# Revit family: Equinox_168 Indirect + trim
name_source: partatom
category: Lighting Fixtures
revit_build: Autodesk Revit 2018 (Build: 20170223_1515(x64)
units: mm (PartAtom-declared; Revit-internal decimal feet)

## family parameters
Cut with Voids When Loaded = No
Host = Face
Light Source = Yes
OmniClass Number = 23.80.70.00
OmniClass Title = Lighting
Part Type = Normal
Room Calculation Point = No
Round Connector Dimension = Use Diameter
Shared = No

## types (1)
- 2059936 EQNX 165 2300 930 SSC
    Apparent Load = 20 VA
    Assembly Code = D5020200
    AssetType = Fixed
    ClassificationName = Uniclass2015
    ClassificationValue = EF_70_80
    Color Filter = 16777215
    Cost = 0 $
    Default Elevation = 1219 mm
    Description = Equinox is an elegant and innovative luminaire designed using the latest optical technology. It is a high quality and efficient lighting solution for office, hospitality, and retail environments. It creates inspirational halo effects regulated by a unique adjustable optic system. It is  Sylsmart dimmable downlight luminaire, Colour rendering index Ra >90, Colour temperature: 3000K Warm White, Class II, Cut out dimensions: 165mm. Low Glare UGR<19.
    Dimming Lamp Color Temperature Shift = <None>
    DocumentationLiterature = http://www.sylvania-lighting.com
    DurationUnit = hours
    ElectricShockClassification = 115
    Emit Shape Visible in Rendering = No
    Emit from Circle Diameter = 610 mm
    ExpectedLife = 50000
    Height (Max) = 162 mm  [stored 0.531496 ft]
    Height (Min) = 99 mm  [stored 0.324803 ft]
    IfcExportAs = Class II
    IfcExportType = IfcLightFixtureType
    ImpactProtectionIndex = IfcLightFixtureType
    IngressProtection = IfcLightFixtureType
    InputNominalFrequency = 3000
    InputVoltage = 0
    LampColourRenderingIndex = 16500
    LampColourTemperature = LED
    LampMacAdamStep = 90
    LampNominalLuminous = 3000 K
    LightOutputRatio = LED
    LuminaireType = 0
    ManufacturerName = 115 lm/W
    Material = Feilo Sylvania
    Material_1_FEILO = <By Category>
    Material_2_FEILO = <By Category>
    Material_3_FEILO = <By Category>
    Material_4_FEILO = <By Category>
    Model = EQUINOX 165 2300 930 SSC
    ModelNumber = 2059936
    ModelReference = EQUINOX 165 2300 930 SSC
    Name = EQUINOX 165 2300 930 SSC
    NominalDepth = 0 mm  [stored 0 ft]
    NominalHeight = 0 mm  [stored 0 ft]
    NominalLength = 0 mm  [stored 0 ft]
    Photometric Web File = 2059936-OD.ies
    PowerConsumption = Lighting
    PowerFactor = 0
    Tilt Angle = 90.00°
    Type Image = <None>
    TypeName = EQUINOX 165 2300 930 SSC
    URL = 0.96
    Voltage = 0 V
    WarrantyDescription = http://www.sylvania-lighting.com
    body diameter = 145 mm
    cut-out = 153 mm

note: [stored X ft] marks values corroborated as IEEE doubles in the binary element streams (Revit-internal decimal feet)

## geometry (parser evidence)
native form markers: Sweep x2
no freeform markers — native parametric forms only
